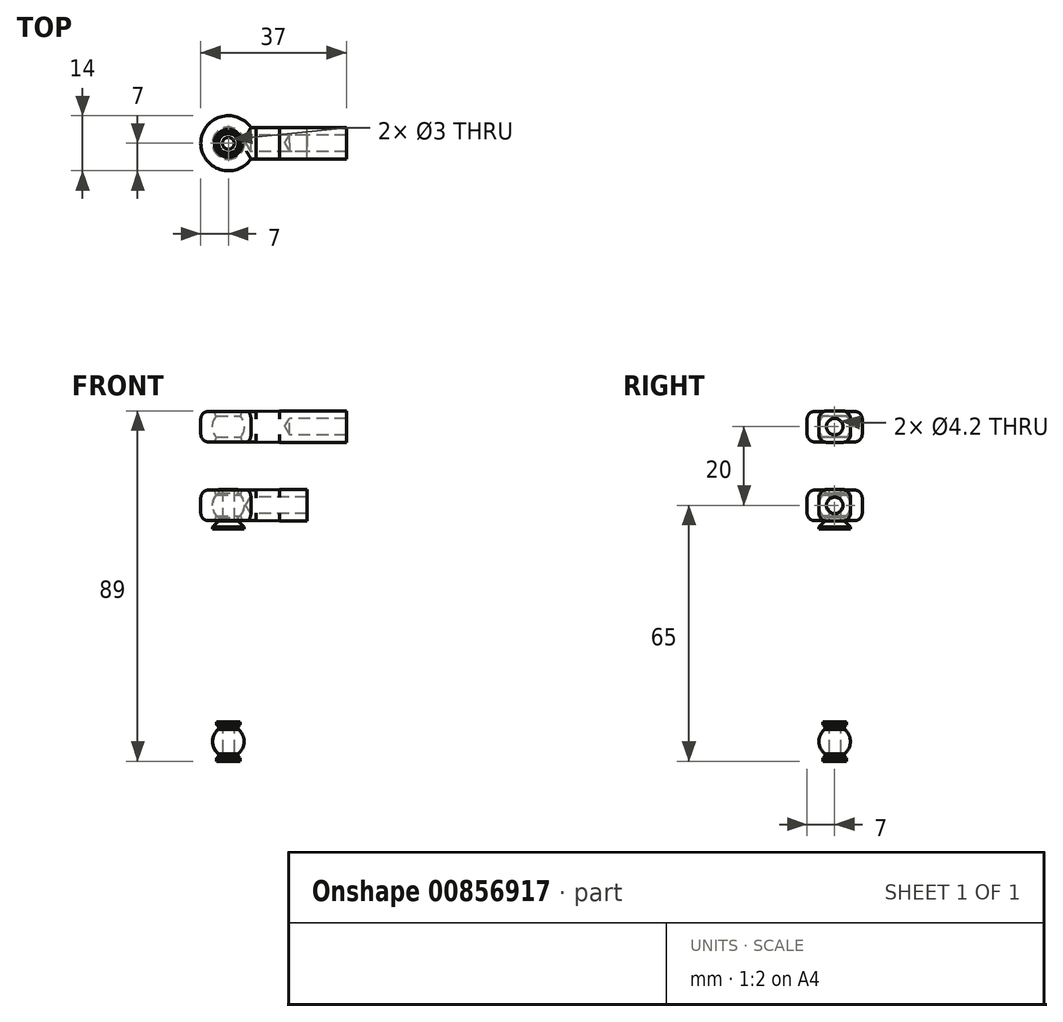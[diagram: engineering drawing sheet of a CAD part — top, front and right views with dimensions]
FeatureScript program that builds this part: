
annotation { "Feature Type Name" : "Feature", "Feature Type Description" : "" }
export const myFeature = defineFeature(function(context is Context, id is Id, definition is map)
    precondition{}
    {
        {
            var Q0;
            Q0=qCreatedBy(makeId("Front.planeOp"),FACE);
            var sketch = newSketch(context, id + "F0", { "sketchPlane" : qUnion([Q0])});
            skArc(sketch, "E0", {"start": v(2.5, -3.12) * mm, "mid": v(4, 0) * mm, "end": v(2.5, 3.12) * mm});
            skLineSegment(sketch, "E1", {"start": v(1.5, 4) * mm, "end": v(2.5, 4) * mm});
            skLineSegment(sketch, "E2", {"start": v(2.5, 4) * mm, "end": v(2.5, 3.12) * mm});
            skLineSegment(sketch, "E3", {"start": v(1.5, 4) * mm, "end": v(1.5, -6) * mm});
            skLineSegment(sketch, "E4", {"start": v(2.5, -4) * mm, "end": v(1.5, -4) * mm, "construction": true});
            skLineSegment(sketch, "E5.trimOffspring", {"start": v(2.5, -3.12) * mm, "end": v(2.5, -4) * mm});
            skLineSegment(sketch, "E6", {"start": v(0, 0) * mm, "end": v(0, 7.62) * mm, "construction": true});
            skLineSegment(sketch, "E7", {"start": v(0, 0) * mm, "end": v(8.34, 0) * mm, "construction": true});
            skPoint(sketch, "E7.endSnap0", {"position": v(1.5, 0) * mm});
            skLineSegment(sketch, "E8", {"start": v(2.5, -4) * mm, "end": v(4, -6) * mm, "construction": true});
            skLineSegment(sketch, "E9", {"start": v(4, -6) * mm, "end": v(1.5, -6) * mm});
            skPoint(sketch, "E10.orphan", {"position": v(0, -6) * mm});
            skLineSegment(sketch, "E11", {"start": v(4, -6) * mm, "end": v(4, -5.5) * mm});
            skLineSegment(sketch, "E12", {"start": v(4, -5.5) * mm, "end": v(2.5, -4) * mm});
            skSolve(sketch);
        }
        {
            var Q0;
            Q0 = qSketchRegion(id + "F0", true);
            var Q1;
            Q1=sQuery(id+"F0.wireOp",EDGE,"E6");
            revolve(context, id + "F1", {"surfaceOperationType" : NewSurfaceOperationType.NEW, "entities" : qUnion([Q0]), "axis" : qUnion([Q1]), "revolveType" : RevolveType.FULL});
        }
        {
            var Q0;
            Q0=qCreatedBy(makeId("Front.planeOp"),FACE);
            var sketch = newSketch(context, id + "F2", { "sketchPlane" : qUnion([Q0])});
            skArc(sketch, "E13.0", {"start": v(3.1, -2.68) * mm, "mid": v(4.1, 0) * mm, "end": v(3.1, 2.68) * mm});
            skLineSegment(sketch, "E14", {"start": v(3.55, 3.9) * mm, "end": v(7, 3.9) * mm});
            skLineSegment(sketch, "E15", {"start": v(7, 3.9) * mm, "end": v(7, -3.9) * mm});
            skLineSegment(sketch, "E16", {"start": v(7, -3.9) * mm, "end": v(3.55, -3.9) * mm});
            skLineSegment(sketch, "E17", {"start": v(0, 0) * mm, "end": v(2.53, 6.95) * mm, "construction": true});
            skLineSegment(sketch, "E18", {"start": v(0, 0) * mm, "end": v(2.64, -7.26) * mm, "construction": true});
            skLineSegment(sketch, "E19.trimOffspring", {"start": v(3.1, -2.68) * mm, "end": v(3.55, -3.9) * mm});
            skLineSegment(sketch, "E20.trimOffspring", {"start": v(3.1, 2.68) * mm, "end": v(3.55, 3.9) * mm});
            skSolve(sketch);
        }
        {
            var Q0;
            Q0 = qSketchRegion(id + "F2", true);
            var Q1;
            Q1=sQuery(id+"F0.wireOp",EDGE,"E6");
            revolve(context, id + "F3", {"surfaceOperationType" : NewSurfaceOperationType.NEW, "entities" : qUnion([Q0]), "axis" : qUnion([Q1]), "revolveType" : RevolveType.FULL});
        }
        {
            var Q0;
            Q0=qCreatedBy(makeId("Front.planeOp"),FACE);
            var sketch = newSketch(context, id + "F4", { "sketchPlane" : qUnion([Q0])});
            skLineSegment(sketch, "E21.bottom", {"start": v(13, 4) * mm, "end": v(20, 4) * mm});
            skLineSegment(sketch, "E21.top", {"start": v(13, -4) * mm, "end": v(20, -4) * mm});
            skLineSegment(sketch, "E21.left", {"start": v(13, 4) * mm, "end": v(13, -4) * mm, "construction": true});
            skLineSegment(sketch, "E21.right", {"start": v(20, 4) * mm, "end": v(20, -4) * mm});
            skPoint(sketch, "E21.middle", {"position": v(16.5, 0) * mm});
            skLineSegment(sketch, "E22", {"start": v(7, 3.9) * mm, "end": v(7, -3.9) * mm, "construction": true});
            skLineSegment(sketch, "E23", {"start": v(13, 4) * mm, "end": v(7, 3.9) * mm});
            skLineSegment(sketch, "E24", {"start": v(13, -4) * mm, "end": v(7, -3.9) * mm});
            skLineSegment(sketch, "E25", {"start": v(5, -3.9) * mm, "end": v(5, 3.9) * mm});
            skLineSegment(sketch, "E26", {"start": v(5, 3.9) * mm, "end": v(7, 3.9) * mm});
            skLineSegment(sketch, "E27", {"start": v(5, -3.9) * mm, "end": v(7, -3.9) * mm});
            skSolve(sketch);
        }
        {
            var Q0;
            Q0 = qSketchRegion(id + "F4", true);
            extrude(context, id + "F5", {"entities" : qUnion([Q0]), "operationType" : NewBodyOperationType.ADD, "depth" : 8 * mm, "offsetDistance" : 25 * mm, "symmetric" : true});
        }
        {
            var Q0;
            Q0=makeQuery(id+"F5.opExtrude","CAP_EDGE",EDGE,{"disambiguationData":[OSD([sQuery(id+"F4.wireOp",EDGE,"E21.bottom")])],"isStart":false});
            var Q1;
            Q1=makeQuery(id+"F3.opRevolve","SWEPT_EDGE",EDGE,{"disambiguationData":[OSD([sQuery(id+"F2.wireOp",EDGE,"E14"),sQuery(id+"F2.wireOp",EDGE,"E15")])]});
            var Q2;
            Q2=makeQuery(id+"F5.opExtrude","CAP_EDGE",EDGE,{"disambiguationData":[OSD([sQuery(id+"F4.wireOp",EDGE,"E21.bottom")])],"isStart":true});
            var Q3;
            Q3=makeQuery(id+"F5.opExtrude","CAP_EDGE",EDGE,{"disambiguationData":[OSD([sQuery(id+"F4.wireOp",EDGE,"E21.top")])],"isStart":true});
            var Q4;
            Q4=makeQuery(id+"F3.opRevolve","SWEPT_EDGE",EDGE,{"disambiguationData":[OSD([sQuery(id+"F2.wireOp",EDGE,"E15"),sQuery(id+"F2.wireOp",EDGE,"E16")])]});
            var Q5;
            Q5=makeQuery(id+"F5.opExtrude","CAP_EDGE",EDGE,{"disambiguationData":[OSD([sQuery(id+"F4.wireOp",EDGE,"E21.top")])],"isStart":false});
            fillet(context, id + "F6", {"entities" : qUnion([Q0, Q1, Q2, Q3, Q4, Q5]), "radius" : 2 * mm, "tangentPropagation" : true, "allowEdgeOverflow" : false});
        }
        {
            var Q0;
            Q0=makeQuery(id+"F5.opExtrude","SWEPT_FACE",FACE,{"disambiguationData":[OSD([sQuery(id+"F4.wireOp",EDGE,"E21.right")])]});
            var sketch = newSketch(context, id + "F7", { "sketchPlane" : qUnion([Q0])});
            skPoint(sketch, "E28", {"position": v(0, 0) * mm});
            skSolve(sketch);
        }
        {
            var Q0;
            Q0=makeQuery(id+"F3.opRevolve","SWEPT_BODY",BODY,{"disambiguationData":[OSD([sQuery(id+"F2.wireOp",EDGE,"E13.0"),sQuery(id+"F2.wireOp",EDGE,"E14"),sQuery(id+"F2.wireOp",EDGE,"E15"),sQuery(id+"F2.wireOp",EDGE,"E16"),sQuery(id+"F2.wireOp",EDGE,"E19.trimOffspring"),sQuery(id+"F2.wireOp",EDGE,"E20.trimOffspring")])]});
            transform(context, id + "F8", {"entities" : qUnion([Q0]), "transformType" : TransformType.TRANSLATION_3D, "dx" : 0 * mm, "dy" : 0 * mm, "dz" : 20 * mm, "makeCopy" : true});
        }
        {
            var Q0;
            Q0=makeQuery(id+"F8.opPattern","COPY",FACE,{"derivedFrom":makeQuery(id+"F5.opExtrude","SWEPT_FACE",FACE,{"disambiguationData":[OSD([sQuery(id+"F4.wireOp",EDGE,"E21.right")])]}),"instanceName":"1"});
            extrude(context, id + "F9", {"entities" : qUnion([Q0]), "operationType" : NewBodyOperationType.ADD, "depth" : 10 * mm, "offsetDistance" : 25 * mm});
        }
        {
            var Q0;
            Q0=makeQuery(id+"F9.opExtrude","CAP_FACE",FACE,{"disambiguationData":[OSD([sQuery(id+"F4.wireOp",EDGE,"E21.right")])],"isStart":false});
            var sketch = newSketch(context, id + "F10", { "sketchPlane" : qUnion([Q0])});
            skPoint(sketch, "E29", {"position": v(0, 20) * mm});
            skPoint(sketch, "E29.positionSnap0", {"position": v(4, 20) * mm});
            skPoint(sketch, "E29.positionSnap1", {"position": v(0, 24) * mm});
            skSolve(sketch);
        }
        {
            var Q0;
            Q0=sQuery(id+"F10.wireOp",VERTEX,"E29");
            var Q1;
            Q1=sQuery(id+"F7.wireOp",VERTEX,"E28");
            var Q2;
            Q2=makeQuery(id+"F3.opRevolve","SWEPT_BODY",BODY,{"disambiguationData":[OSD([sQuery(id+"F2.wireOp",EDGE,"E13.0"),sQuery(id+"F2.wireOp",EDGE,"E14"),sQuery(id+"F2.wireOp",EDGE,"E15"),sQuery(id+"F2.wireOp",EDGE,"E16"),sQuery(id+"F2.wireOp",EDGE,"E19.trimOffspring"),sQuery(id+"F2.wireOp",EDGE,"E20.trimOffspring")])]});
            var Q3;
            Q3=makeQuery(id+"F8.opPattern","COPY",BODY,{"derivedFrom":makeQuery(id+"F3.opRevolve","SWEPT_BODY",BODY,{"disambiguationData":[OSD([sQuery(id+"F2.wireOp",EDGE,"E13.0"),sQuery(id+"F2.wireOp",EDGE,"E14"),sQuery(id+"F2.wireOp",EDGE,"E15"),sQuery(id+"F2.wireOp",EDGE,"E16"),sQuery(id+"F2.wireOp",EDGE,"E19.trimOffspring"),sQuery(id+"F2.wireOp",EDGE,"E20.trimOffspring")])]}),"instanceName":"1"});
            hole(context, id + "F11", {"style" : HoleStyle.SIMPLE, "endStyle" : HoleEndStyle.BLIND, "standardTappedOrClearance" : lookupTablePath({ "standard" : "ISO", "engagement" : "75%", "pitch" : "0.8 mm", "size" : "M5", "type" : "Tapped" }), "standardBlindInLast" : lookupTablePath({ "standard" : "ISO", "engagement" : "75%", "pitch" : "0.8 mm", "size" : "M5", "type" : "Tapped" }), "holeDiameter" : 4.2 * mm, "majorDiameter" : 5 * mm, "showTappedDepth" : true, "holeDepth" : 14.4 * mm, "isTappedThrough" : true, "tappedDepth" : 12 * mm, "tapClearance" : 3, "locations" : qUnion([Q0, Q1]), "scope" : qUnion([Q2, Q3])});
        }
        {
            var Q0;
            Q0=qCreatedBy(makeId("Front.planeOp"),FACE);
            var sketch = newSketch(context, id + "F12", { "sketchPlane" : qUnion([Q0])});
            skArc(sketch, "E30", {"start": v(2.5, -63.12) * mm, "mid": v(4, -60) * mm, "end": v(2.5, -56.88) * mm});
            skLineSegment(sketch, "E31", {"start": v(1.5, -56) * mm, "end": v(2.5, -56) * mm, "construction": true});
            skLineSegment(sketch, "E32", {"start": v(2.5, -56) * mm, "end": v(2.5, -56.88) * mm});
            skLineSegment(sketch, "E33", {"start": v(1.5, -55) * mm, "end": v(1.5, -65) * mm});
            skLineSegment(sketch, "E34", {"start": v(2.5, -64) * mm, "end": v(1.5, -64) * mm, "construction": true});
            skLineSegment(sketch, "E35.trimOffspring", {"start": v(2.5, -63.12) * mm, "end": v(2.5, -64) * mm});
            skLineSegment(sketch, "E36", {"start": v(0, -60) * mm, "end": v(0, -14.76) * mm, "construction": true});
            skLineSegment(sketch, "E37", {"start": v(-42.77, -60) * mm, "end": v(0, -60) * mm, "construction": true});
            skPoint(sketch, "E37.endSnap0", {"position": v(1.5, -60) * mm});
            skLineSegment(sketch, "E38", {"start": v(2.5, -64) * mm, "end": v(3, -64.2) * mm});
            skLineSegment(sketch, "E39", {"start": v(3, -64.2) * mm, "end": v(3, -65) * mm});
            skLineSegment(sketch, "E40", {"start": v(3, -65) * mm, "end": v(1.5, -65) * mm});
            skLineSegment(sketch, "E41", {"start": v(2.5, -56) * mm, "end": v(3, -55.8) * mm});
            skLineSegment(sketch, "E42", {"start": v(3, -55.8) * mm, "end": v(3, -55) * mm});
            skLineSegment(sketch, "E43", {"start": v(3, -55) * mm, "end": v(1.5, -55) * mm});
            skPoint(sketch, "E44.orphan", {"position": v(0, -65) * mm});
            skSolve(sketch);
        }
        {
            var Q0;
            Q0=makeQuery(id+"F12.imprint","IMPRINT",FACE,{"disambiguationData":[TD([[makeQuery(id+"F12.imprint","IMPRINT",EDGE,{"derivedFrom":sQuery(id+"F12.wireOp",EDGE,"E30")}),1.0]])]});
            var Q1;
            Q1=sQuery(id+"F12.wireOp",EDGE,"E36");
            revolve(context, id + "F13", {"surfaceOperationType" : NewSurfaceOperationType.NEW, "entities" : qUnion([Q0]), "axis" : qUnion([Q1]), "revolveType" : RevolveType.FULL});
        }
    });
